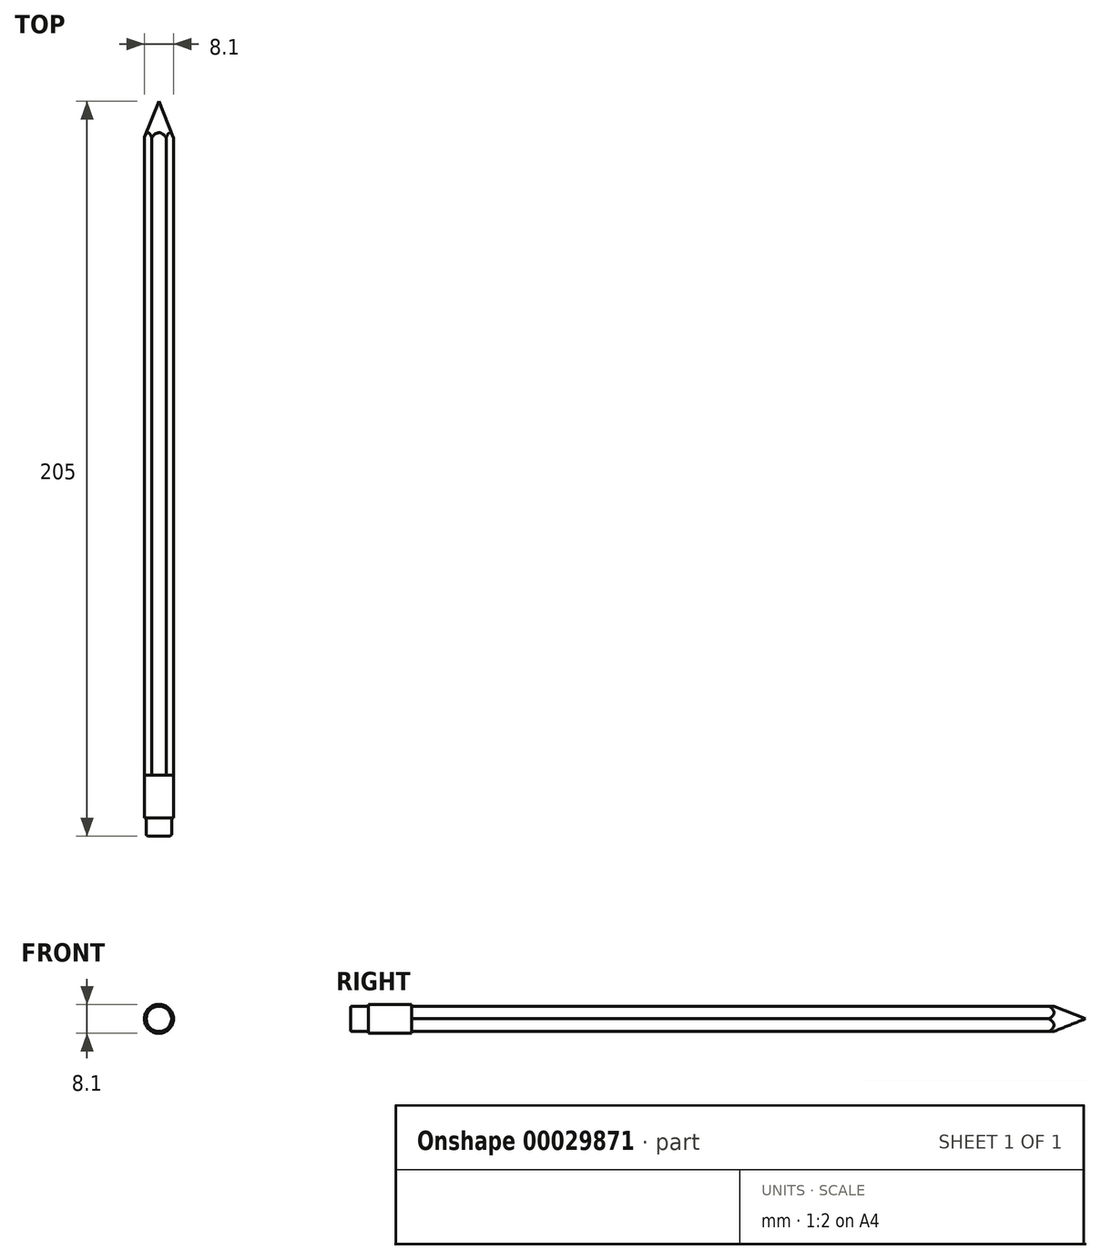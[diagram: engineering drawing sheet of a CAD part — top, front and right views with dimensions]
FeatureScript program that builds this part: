
annotation { "Feature Type Name" : "Feature", "Feature Type Description" : "" }
export const myFeature = defineFeature(function(context is Context, id is Id, definition is map)
    precondition{}
    {
        {
            var Q0;
            Q0=qCreatedBy(makeId("Front.planeOp"),FACE);
            var sketch = newSketch(context, id + "F0", { "sketchPlane" : qUnion([Q0])});
            skCircle(sketch, "E0.cCircle", {"center": v(0, 0) * mm, "radius": 3.5 * mm, "construction": true});
            skLineSegment(sketch, "E0.0", {"start": v(2.02, -3.5) * mm, "end": v(-2.02, -3.5) * mm});
            skLineSegment(sketch, "E0.1", {"start": v(-2.02, -3.5) * mm, "end": v(-4.04, 0) * mm});
            skLineSegment(sketch, "E0.2", {"start": v(-4.04, 0) * mm, "end": v(-2.02, 3.5) * mm});
            skLineSegment(sketch, "E0.3", {"start": v(-2.02, 3.5) * mm, "end": v(2.02, 3.5) * mm});
            skLineSegment(sketch, "E0.4", {"start": v(2.02, 3.5) * mm, "end": v(4.04, 0) * mm});
            skLineSegment(sketch, "E0.5", {"start": v(4.04, 0) * mm, "end": v(2.02, -3.5) * mm});
            skPoint(sketch, "E0.0.midPoint", {"position": v(0, -3.5) * mm});
            skSolve(sketch);
        }
        {
            var Q0;
            Q0 = qSketchRegion(id + "F0", true);
            extrude(context, id + "F1", {"entities" : qUnion([Q0]), "depth" : 190 * mm});
        }
        {
            var Q0;
            Q0=qCreatedBy(makeId("Top.planeOp"),FACE);
            var sketch = newSketch(context, id + "F2", { "sketchPlane" : qUnion([Q0])});
            skLineSegment(sketch, "E1", {"start": v(0, 0) * mm, "end": v(-4, 0) * mm});
            skLineSegment(sketch, "E2", {"start": v(-4, 0) * mm, "end": v(0, 10) * mm});
            skLineSegment(sketch, "E3", {"start": v(0, 10) * mm, "end": v(0, 0) * mm});
            skSolve(sketch);
        }
        {
            var Q0;
            Q0=makeQuery(id+"F2.imprint","IMPRINT",FACE,{"disambiguationData":[TD([[makeQuery(id+"F2.imprint","IMPRINT",EDGE,{"derivedFrom":sQuery(id+"F2.wireOp",EDGE,"E1")}),-1.0]])]});
            var Q1;
            Q1=sQuery(id+"F2.wireOp",EDGE,"E3");
            revolve(context, id + "F3", {"operationType" : NewBodyOperationType.ADD, "entities" : qUnion([Q0]), "axis" : qUnion([Q1]), "revolveType" : RevolveType.FULL});
        }
        {
            var Q0;
            Q0=makeQuery(id+"F1.opExtrude","CAP_FACE",FACE,{"disambiguationData":[OSD([sQuery(id+"F0.wireOp",EDGE,"E0.0"),sQuery(id+"F0.wireOp",EDGE,"E0.1"),sQuery(id+"F0.wireOp",EDGE,"E0.2"),sQuery(id+"F0.wireOp",EDGE,"E0.3"),sQuery(id+"F0.wireOp",EDGE,"E0.4"),sQuery(id+"F0.wireOp",EDGE,"E0.5")])],"isStart":false});
            var sketch = newSketch(context, id + "F4", { "sketchPlane" : qUnion([Q0])});
            skLineSegment(sketch, "E4", {"start": v(-2.02, 3.5) * mm, "end": v(2.02, 3.5) * mm});
            skLineSegment(sketch, "E5", {"start": v(4.04, 0) * mm, "end": v(2.02, -3.5) * mm});
            skLineSegment(sketch, "E6", {"start": v(2.02, -3.5) * mm, "end": v(-2.02, -3.5) * mm});
            skLineSegment(sketch, "E7", {"start": v(-2.02, -3.5) * mm, "end": v(-4.04, 0) * mm});
            skLineSegment(sketch, "E8", {"start": v(-4.04, 0) * mm, "end": v(-2.02, 3.5) * mm});
            skCircle(sketch, "E9", {"center": v(0, 0) * mm, "radius": 5.12 * mm});
            skSolve(sketch);
        }
        {
            var Q0;
            Q0=makeQuery(id+"F4.imprint","IMPRINT",FACE,{"disambiguationData":[TD([[makeQuery(id+"F4.imprint","IMPRINT",EDGE,{"derivedFrom":sQuery(id+"F4.wireOp",EDGE,"E4")}),1.0]])]});
            extrude(context, id + "F5", {"entities" : qUnion([Q0]), "operationType" : NewBodyOperationType.REMOVE, "endBound" : BoundingType.THROUGH_ALL, "oppositeDirection" : true, "depth" : 25 * mm});
        }
        {
            var Q0;
            Q0=makeQuery(id+"F1.opExtrude","CAP_FACE",FACE,{"disambiguationData":[OSD([sQuery(id+"F0.wireOp",EDGE,"E0.0"),sQuery(id+"F0.wireOp",EDGE,"E0.1"),sQuery(id+"F0.wireOp",EDGE,"E0.2"),sQuery(id+"F0.wireOp",EDGE,"E0.3"),sQuery(id+"F0.wireOp",EDGE,"E0.4"),sQuery(id+"F0.wireOp",EDGE,"E0.5")])],"isStart":false});
            var sketch = newSketch(context, id + "F6", { "sketchPlane" : qUnion([Q0])});
            skCircle(sketch, "E10", {"center": v(0, 0) * mm, "radius": 4.05 * mm});
            skSolve(sketch);
        }
        {
            var Q0;
            Q0 = qSketchRegion(id + "F6", true);
            extrude(context, id + "F7", {"entities" : qUnion([Q0]), "operationType" : NewBodyOperationType.ADD, "oppositeDirection" : true, "depth" : 12 * mm});
        }
        {
            var Q0;
            Q0=makeQuery(id+"F7.boolean.opBoolean","MERGE",FACE,{"derivedFrom":[makeQuery(id+"F1.opExtrude","CAP_FACE",FACE,{"disambiguationData":[OSD([sQuery(id+"F0.wireOp",EDGE,"E0.0"),sQuery(id+"F0.wireOp",EDGE,"E0.1"),sQuery(id+"F0.wireOp",EDGE,"E0.2"),sQuery(id+"F0.wireOp",EDGE,"E0.3"),sQuery(id+"F0.wireOp",EDGE,"E0.4"),sQuery(id+"F0.wireOp",EDGE,"E0.5")])],"isStart":false}),makeQuery(id+"F7.opExtrude","CAP_FACE",FACE,{"disambiguationData":[OSD([sQuery(id+"F6.wireOp",EDGE,"E10")])],"isStart":true})]});
            var sketch = newSketch(context, id + "F8", { "sketchPlane" : qUnion([Q0])});
            skCircle(sketch, "E11", {"center": v(0, 0) * mm, "radius": 3.54 * mm});
            skSolve(sketch);
        }
        {
            var Q0;
            Q0 = qSketchRegion(id + "F8", true);
            extrude(context, id + "F9", {"entities" : qUnion([Q0]), "operationType" : NewBodyOperationType.ADD, "depth" : 5 * mm});
        }
        {
            var Q0;
            Q0=makeQuery(id+"F9.opExtrude","CAP_EDGE",EDGE,{"disambiguationData":[OSD([sQuery(id+"F8.wireOp",EDGE,"E11")])],"isStart":false});
            fillet(context, id + "F10", {"entities" : qUnion([Q0]), "radius" : .5 * mm, "tangentPropagation" : true, "allowEdgeOverflow" : false});
        }
    });
